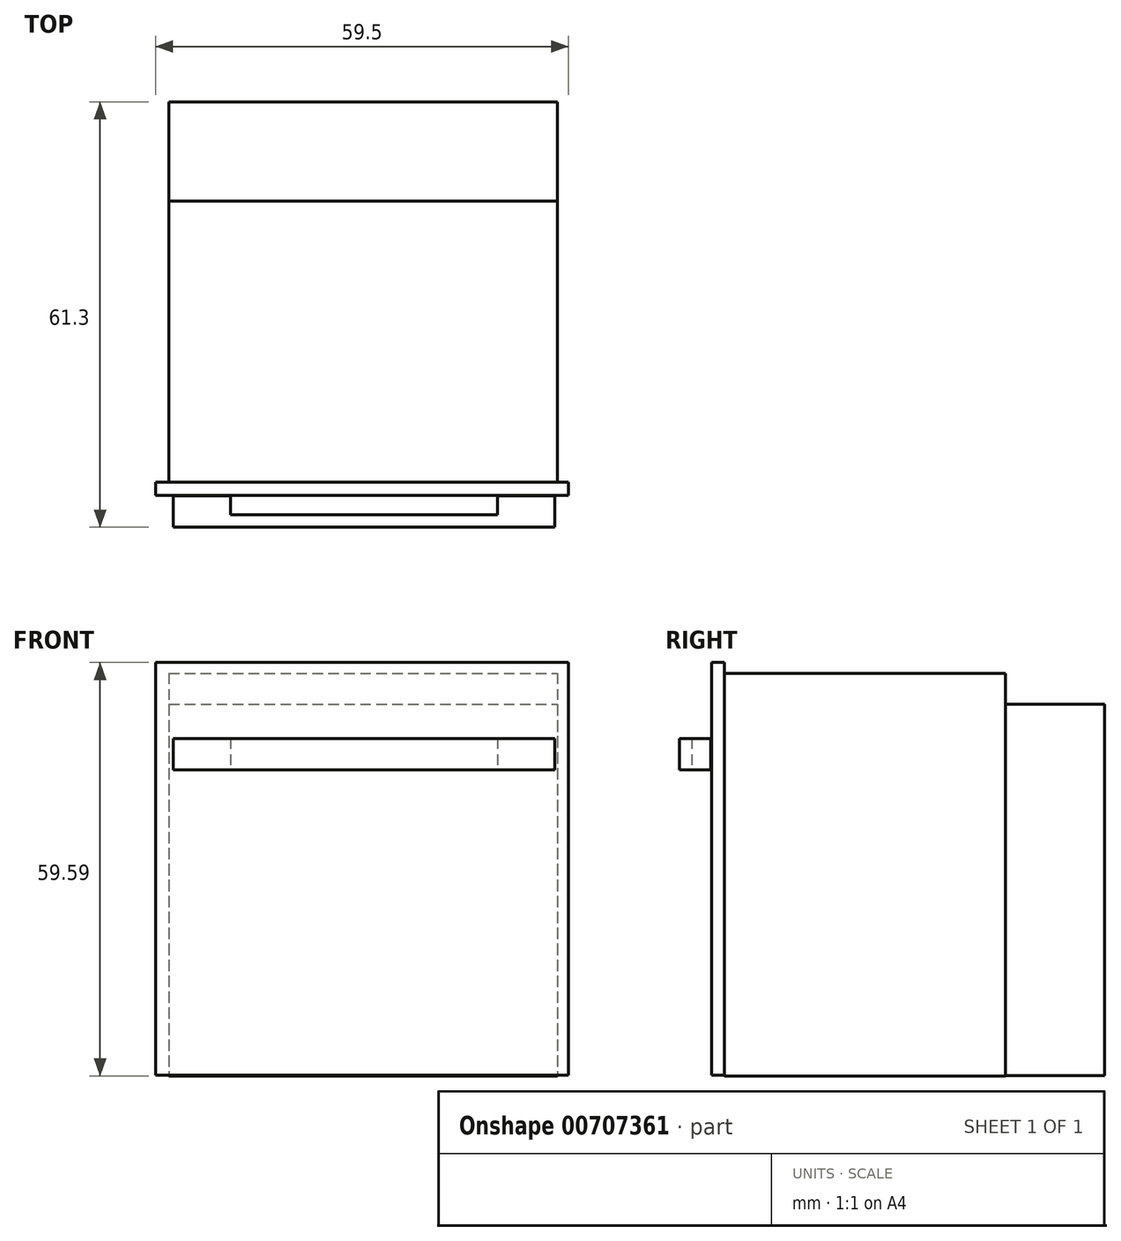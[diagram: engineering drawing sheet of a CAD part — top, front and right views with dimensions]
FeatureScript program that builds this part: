
annotation { "Feature Type Name" : "Feature", "Feature Type Description" : "" }
export const myFeature = defineFeature(function(context is Context, id is Id, definition is map)
    precondition{}
    {
        {
            var Q0;
            Q0=qCreatedBy(makeId("Front.planeOp"),FACE);
            var sketch = newSketch(context, id + "F0", { "sketchPlane" : qUnion([Q0])});
            skLineSegment(sketch, "E0.bottom", {"start": v(-27.15, 28.19) * mm, "end": v(28.85, 28.19) * mm});
            skLineSegment(sketch, "E0.top", {"start": v(-27.15, -29.81) * mm, "end": v(28.85, -29.81) * mm});
            skLineSegment(sketch, "E0.left", {"start": v(-27.15, 28.19) * mm, "end": v(-27.15, -29.81) * mm});
            skLineSegment(sketch, "E0.right", {"start": v(28.85, 28.19) * mm, "end": v(28.85, -29.81) * mm});
            skSolve(sketch);
        }
        {
            var Q0;
            Q0=makeQuery(id+"F0.imprint","IMPRINT",FACE,{"disambiguationData":[TD([[makeQuery(id+"F0.imprint","IMPRINT",EDGE,{"derivedFrom":sQuery(id+"F0.wireOp",EDGE,"E0.bottom")}),-1.0]])]});
            extrude(context, id + "F1", {"entities" : qUnion([Q0]), "depth" : 40.5 * mm});
        }
        {
            var Q0;
            Q0=qCreatedBy(makeId("Front.planeOp"),FACE);
            var sketch = newSketch(context, id + "F2", { "sketchPlane" : qUnion([Q0])});
            skLineSegment(sketch, "E1.bottom", {"start": v(-29.54, 26.56) * mm, "end": v(26.46, 26.56) * mm});
            skLineSegment(sketch, "E1.top", {"start": v(-29.54, -26.94) * mm, "end": v(26.46, -26.94) * mm});
            skLineSegment(sketch, "E1.left", {"start": v(-29.54, 26.56) * mm, "end": v(-29.54, -26.94) * mm});
            skLineSegment(sketch, "E1.right", {"start": v(26.46, 26.56) * mm, "end": v(26.46, -26.94) * mm});
            skSolve(sketch);
        }
        {
            var Q0;
            Q0=qSketchRegion(id+"F2",true);
            extrude(context, id + "F3", {"entities" : qUnion([Q0]), "depth" : 14.3 * mm});
        }
        {
            var Q0;
            Q0=makeQuery(id+"F3.opExtrude","SWEPT_BODY",BODY,{"disambiguationData":[OSD([sQuery(id+"F2.wireOp",EDGE,"E1.bottom"),sQuery(id+"F2.wireOp",EDGE,"E1.top"),sQuery(id+"F2.wireOp",EDGE,"E1.left"),sQuery(id+"F2.wireOp",EDGE,"E1.right")])]});
            var Q1;
            Q1=makeQuery(id+"F3.opExtrude","CAP_FACE",FACE,{"disambiguationData":[OSD([sQuery(id+"F2.wireOp",EDGE,"E1.bottom"),sQuery(id+"F2.wireOp",EDGE,"E1.top"),sQuery(id+"F2.wireOp",EDGE,"E1.left"),sQuery(id+"F2.wireOp",EDGE,"E1.right")])],"isStart":false});
            transform(context, id + "F4", {"entities" : qUnion([Q0]), "transformType" : TransformType.TRANSLATION_DISTANCE, "transformDirection" : qUnion([Q1]), "distance" : 16.5 * mm, "oppositeDirection" : true, "makeCopy" : false});
        }
        {
            var Q0;
            Q0=makeQuery(id+"F3.opExtrude","SWEPT_BODY",BODY,{"disambiguationData":[OSD([sQuery(id+"F2.wireOp",EDGE,"E1.bottom"),sQuery(id+"F2.wireOp",EDGE,"E1.top"),sQuery(id+"F2.wireOp",EDGE,"E1.left"),sQuery(id+"F2.wireOp",EDGE,"E1.right")])]});
            transform(context, id + "F5", {"entities" : qUnion([Q0]), "transformType" : TransformType.TRANSLATION_3D, "dx" : 2.4 * mm, "dy" : -2.2 * mm, "dz" : -2.8 * mm, "makeCopy" : false});
        }
        {
            var Q0;
            Q0=qCreatedBy(makeId("Front.planeOp"),FACE);
            var sketch = newSketch(context, id + "F6", { "sketchPlane" : qUnion([Q0])});
            skLineSegment(sketch, "E2.bottom", {"start": v(-30.65, 29.85) * mm, "end": v(28.85, 29.85) * mm});
            skLineSegment(sketch, "E2.top", {"start": v(-30.65, -29.65) * mm, "end": v(28.85, -29.65) * mm});
            skLineSegment(sketch, "E2.left", {"start": v(-30.65, 29.85) * mm, "end": v(-30.65, -29.65) * mm});
            skLineSegment(sketch, "E2.right", {"start": v(28.85, 29.85) * mm, "end": v(28.85, -29.65) * mm});
            skSolve(sketch);
        }
        {
            var Q0;
            Q0=qSketchRegion(id+"F6",true);
            extrude(context, id + "F7", {"entities" : qUnion([Q0]), "depth" : 1.9 * mm});
        }
        {
            var Q0;
            Q0=makeQuery(id+"F7.opExtrude","SWEPT_BODY",BODY,{"disambiguationData":[OSD([sQuery(id+"F6.wireOp",EDGE,"E2.bottom"),sQuery(id+"F6.wireOp",EDGE,"E2.top"),sQuery(id+"F6.wireOp",EDGE,"E2.left"),sQuery(id+"F6.wireOp",EDGE,"E2.right")])]});
            transform(context, id + "F8", {"entities" : qUnion([Q0]), "transformType" : TransformType.TRANSLATION_3D, "dx" : 1.6 * mm, "dy" : -40.5 * mm, "dz" : -0.07 * mm, "makeCopy" : false});
        }
        {
            var Q0;
            Q0=qCreatedBy(makeId("Front.planeOp"),FACE);
            var sketch = newSketch(context, id + "F9", { "sketchPlane" : qUnion([Q0])});
            skLineSegment(sketch, "E3", {"start": v(-40.02, 11.42) * mm, "end": v(-40.02, 6.92) * mm});
            skLineSegment(sketch, "E4", {"start": v(-40.02, 6.92) * mm, "end": v(14.98, 6.92) * mm});
            skLineSegment(sketch, "E5", {"start": v(14.98, 11.42) * mm, "end": v(6.74, 11.42) * mm});
            skLineSegment(sketch, "E6", {"start": v(6.74, 11.42) * mm, "end": v(6.74, 8.71) * mm});
            skLineSegment(sketch, "E7", {"start": v(6.74, 8.71) * mm, "end": v(-31.78, 8.71) * mm});
            skLineSegment(sketch, "E8", {"start": v(-31.78, 8.71) * mm, "end": v(-31.78, 11.42) * mm});
            skLineSegment(sketch, "E9", {"start": v(-31.78, 11.42) * mm, "end": v(-40.02, 11.42) * mm});
            skLineSegment(sketch, "E10", {"start": v(14.98, 11.42) * mm, "end": v(14.98, 6.92) * mm});
            skSolve(sketch);
        }
        {
            var Q0;
            Q0=makeQuery(id+"F9.imprint","IMPRINT",FACE,{"disambiguationData":[TD([[makeQuery(id+"F9.imprint","IMPRINT",EDGE,{"derivedFrom":sQuery(id+"F9.wireOp",EDGE,"E3")}),1.0]])]});
            extrude(context, id + "F10", {"entities" : qUnion([Q0]), "depth" : 4.5 * mm});
        }
        {
            var Q0;
            Q0=makeQuery(id+"F10.opExtrude","SWEPT_BODY",BODY,{"disambiguationData":[OSD([sQuery(id+"F9.wireOp",EDGE,"E3"),sQuery(id+"F9.wireOp",EDGE,"E4"),sQuery(id+"F9.wireOp",EDGE,"E5"),sQuery(id+"F9.wireOp",EDGE,"E6"),sQuery(id+"F9.wireOp",EDGE,"E7"),sQuery(id+"F9.wireOp",EDGE,"E8"),sQuery(id+"F9.wireOp",EDGE,"E9"),sQuery(id+"F9.wireOp",EDGE,"E10")])]});
            var Q1;
            Q1=makeQuery(id+"F10.opExtrude","CAP_EDGE",EDGE,{"disambiguationData":[OSD([sQuery(id+"F9.wireOp",EDGE,"E5")])],"isStart":false});
            transform(context, id + "F11", {"entities" : qUnion([Q0]), "transformType" : TransformType.ROTATION, "transformAxis" : qUnion([Q1]), "angle" : 90 * degree, "makeCopy" : false});
        }
        {
            var Q0;
            Q0=makeQuery(id+"F10.opExtrude","SWEPT_BODY",BODY,{"disambiguationData":[OSD([sQuery(id+"F9.wireOp",EDGE,"E3"),sQuery(id+"F9.wireOp",EDGE,"E4"),sQuery(id+"F9.wireOp",EDGE,"E5"),sQuery(id+"F9.wireOp",EDGE,"E6"),sQuery(id+"F9.wireOp",EDGE,"E7"),sQuery(id+"F9.wireOp",EDGE,"E8"),sQuery(id+"F9.wireOp",EDGE,"E9"),sQuery(id+"F9.wireOp",EDGE,"E10")])]});
            transform(context, id + "F12", {"entities" : qUnion([Q0]), "transformType" : TransformType.TRANSLATION_3D, "dx" : 13.5 * mm, "dy" : -38 * mm, "dz" : 7.4 * mm, "makeCopy" : false});
        }
    });
